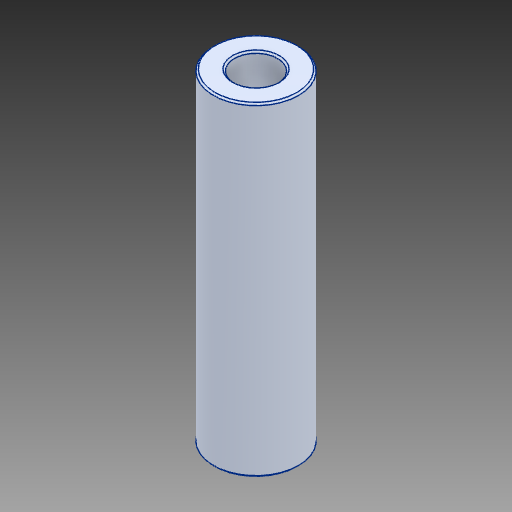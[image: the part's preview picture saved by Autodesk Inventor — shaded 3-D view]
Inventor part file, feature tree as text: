
AUTODESK INVENTOR PART (.ipt)
format: ipt  version: 2017 (Build 210142000, 142)  size: 97,280 bytes
history: mixed  units: mm
features: chamfer x1, imported_body x1
ambient origin geometry x8: Origin, YZ Plane, XZ Plane, XY Plane, X Axis, Y Axis, Z Axis, Center Point
bodies: Solid1 (imported_parasolid)
feature tree (2):
  chamfer  "Chamfer1"  [1 undecoded]
  imported_body  NMx_Import_Brep_tag  [imported B-rep: ~8 faces, bbox_mm=[2.45, 0.0, 38.1]]
note: 1 required parameter value undecoded (feature->parameter linkage not recoverable at this tier; creation-order binding heuristic only, values carry confidence <= 0.55)
